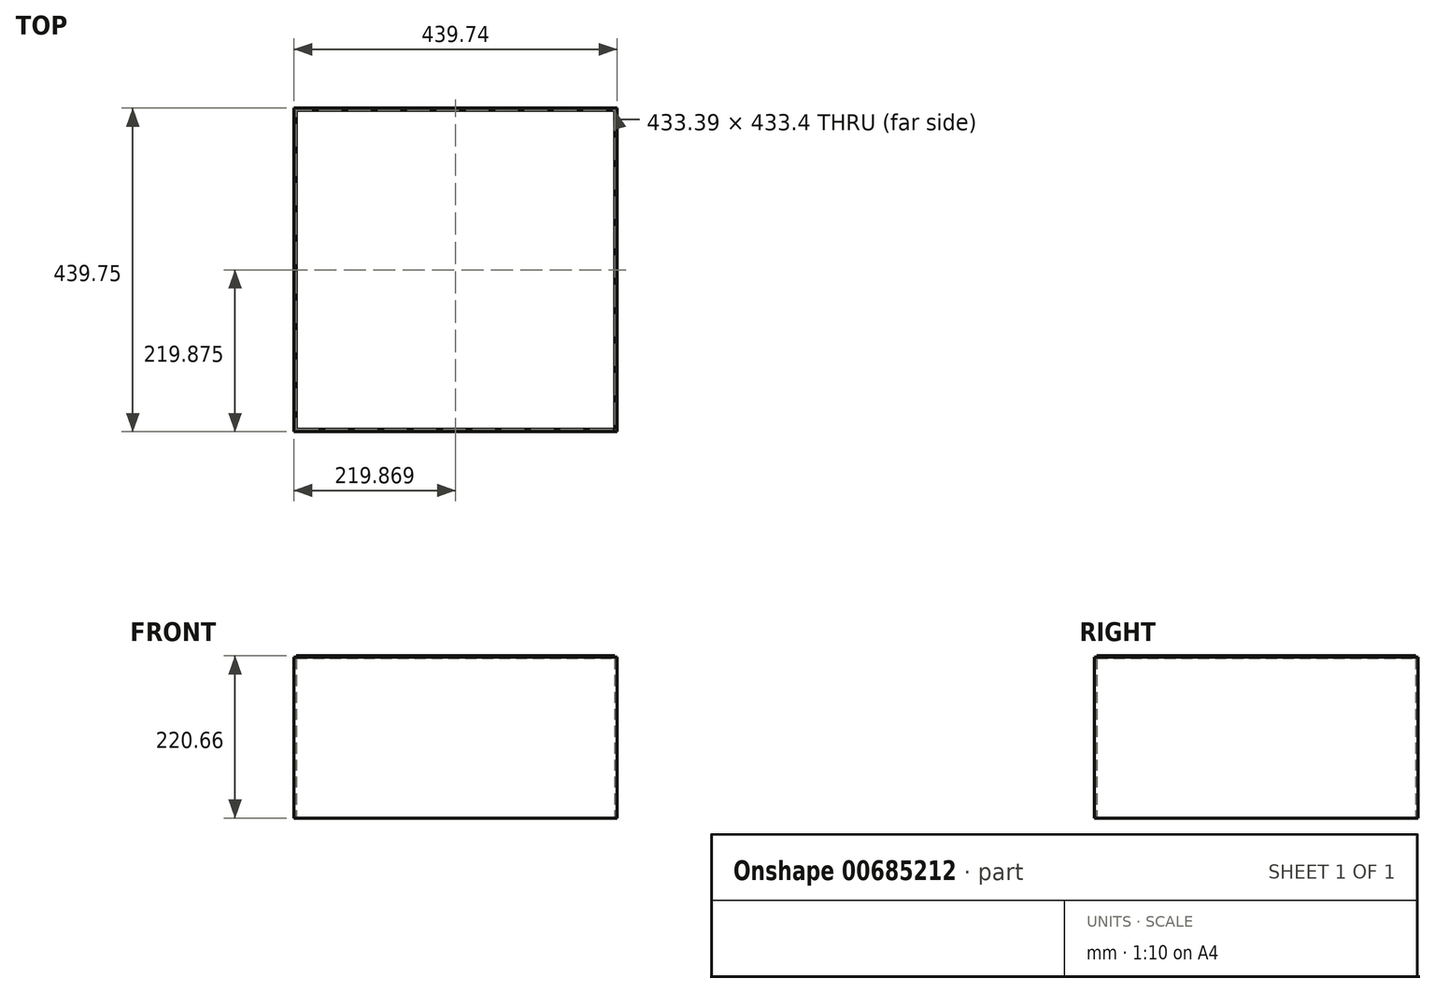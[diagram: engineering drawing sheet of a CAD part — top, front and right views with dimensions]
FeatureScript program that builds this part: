
annotation { "Feature Type Name" : "Feature", "Feature Type Description" : "" }
export const myFeature = defineFeature(function(context is Context, id is Id, definition is map)
    precondition{}
    {
        {
            var Q0;
            Q0=qCreatedBy(makeId("Top.planeOp"),FACE);
            var sketch = newSketch(context, id + "F0", { "sketchPlane" : qUnion([Q0])});
            skLineSegment(sketch, "E0.bottom", {"start": v(0, 0) * mm, "end": v(439.74, 0) * mm});
            skLineSegment(sketch, "E0.top", {"start": v(0, 439.75) * mm, "end": v(439.74, 439.75) * mm});
            skLineSegment(sketch, "E0.left", {"start": v(0, 0) * mm, "end": v(0, 439.75) * mm});
            skLineSegment(sketch, "E0.right", {"start": v(439.74, 0) * mm, "end": v(439.74, 439.75) * mm});
            skLineSegment(sketch, "E1.bottom", {"start": v(3.18, 3.18) * mm, "end": v(436.56, 3.18) * mm});
            skLineSegment(sketch, "E1.top", {"start": v(3.17, 436.58) * mm, "end": v(436.56, 436.58) * mm});
            skLineSegment(sketch, "E1.left", {"start": v(3.17, 3.18) * mm, "end": v(3.17, 436.58) * mm});
            skLineSegment(sketch, "E1.right", {"start": v(436.56, 3.18) * mm, "end": v(436.56, 436.58) * mm});
            skSolve(sketch);
        }
        {
            var Q0;
            Q0=makeQuery(id+"F0.imprint","IMPRINT",FACE,{"disambiguationData":[TD([[makeQuery(id+"F0.imprint","IMPRINT",EDGE,{"derivedFrom":sQuery(id+"F0.wireOp",EDGE,"E0.bottom")}),1.0]])]});
            extrude(context, id + "F1", {"entities" : qUnion([Q0]), "depth" : 219.07 * mm, "offsetDistance" : 25.4 * mm});
        }
        {
            var Q0;
            Q0=makeQuery(id+"F1.opExtrude","CAP_FACE",FACE,{"disambiguationData":[OSD([sQuery(id+"F0.wireOp",EDGE,"E0.bottom"),sQuery(id+"F0.wireOp",EDGE,"E0.top"),sQuery(id+"F0.wireOp",EDGE,"E0.left"),sQuery(id+"F0.wireOp",EDGE,"E0.right"),sQuery(id+"F0.wireOp",EDGE,"E1.bottom"),sQuery(id+"F0.wireOp",EDGE,"E1.top"),sQuery(id+"F0.wireOp",EDGE,"E1.left"),sQuery(id+"F0.wireOp",EDGE,"E1.right")])],"isStart":false});
            var sketch = newSketch(context, id + "F2", { "sketchPlane" : qUnion([Q0])});
            skLineSegment(sketch, "E2.bottom", {"start": v(0, 0) * mm, "end": v(439.74, 0) * mm});
            skLineSegment(sketch, "E2.top", {"start": v(0, 439.75) * mm, "end": v(439.74, 439.75) * mm});
            skLineSegment(sketch, "E2.left", {"start": v(0, 0) * mm, "end": v(0, 439.75) * mm});
            skLineSegment(sketch, "E2.right", {"start": v(439.74, 0) * mm, "end": v(439.74, 439.75) * mm});
            skLineSegment(sketch, "E3.bottom", {"start": v(3.18, 3.18) * mm, "end": v(436.56, 3.18) * mm});
            skLineSegment(sketch, "E3.top", {"start": v(3.18, 436.58) * mm, "end": v(436.56, 436.58) * mm});
            skLineSegment(sketch, "E3.left", {"start": v(3.18, 3.18) * mm, "end": v(3.18, 436.58) * mm});
            skLineSegment(sketch, "E3.right", {"start": v(436.56, 3.18) * mm, "end": v(436.56, 436.58) * mm});
            skSolve(sketch);
        }
        {
            var Q0;
            Q0=makeQuery(id+"F2.imprint","IMPRINT",FACE,{"disambiguationData":[TD([[makeQuery(id+"F2.imprint","IMPRINT",EDGE,{"derivedFrom":sQuery(id+"F2.wireOp",EDGE,"E3.bottom")}),1.0]])]});
            extrude(context, id + "F3", {"entities" : qUnion([Q0]), "operationType" : NewBodyOperationType.ADD, "endBound" : BoundingType.SYMMETRIC, "depth" : 3.17 * mm, "offsetDistance" : 25.4 * mm});
        }
    });
